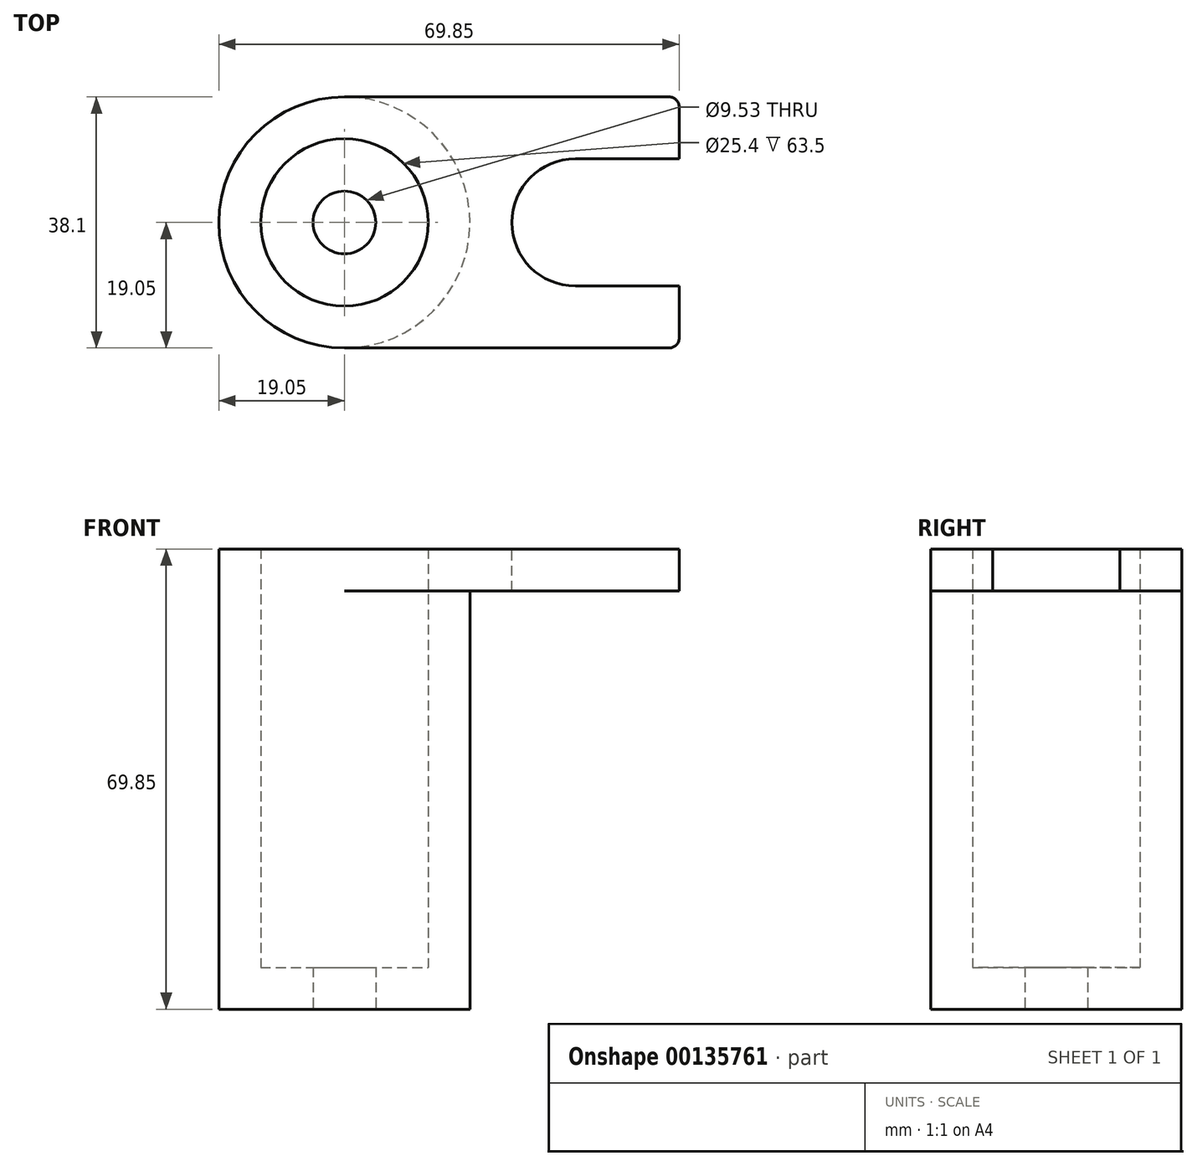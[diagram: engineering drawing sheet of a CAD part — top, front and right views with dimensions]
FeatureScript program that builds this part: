
annotation { "Feature Type Name" : "Feature", "Feature Type Description" : "" }
export const myFeature = defineFeature(function(context is Context, id is Id, definition is map)
    precondition{}
    {
        {
            var Q0;
            Q0=qCreatedBy(makeId("Front.planeOp"),FACE);
            var sketch = newSketch(context, id + "F0", { "sketchPlane" : qUnion([Q0])});
            skLineSegment(sketch, "E0", {"start": v(0, 0) * mm, "end": v(4.76, 0) * mm, "construction": true});
            skLineSegment(sketch, "E1", {"start": v(4.76, 0) * mm, "end": v(19.05, 0) * mm});
            skLineSegment(sketch, "E2", {"start": v(19.05, 0) * mm, "end": v(19.05, 69.85) * mm});
            skLineSegment(sketch, "E3", {"start": v(19.05, 69.85) * mm, "end": v(12.7, 69.85) * mm});
            skLineSegment(sketch, "E4", {"start": v(12.7, 69.85) * mm, "end": v(12.7, 6.35) * mm});
            skLineSegment(sketch, "E5", {"start": v(12.7, 6.35) * mm, "end": v(4.76, 6.35) * mm});
            skLineSegment(sketch, "E6", {"start": v(4.76, 6.35) * mm, "end": v(4.76, 0) * mm});
            skLineSegment(sketch, "E7", {"start": v(0, 0) * mm, "end": v(0, 69.85) * mm, "construction": true});
            skSolve(sketch);
        }
        {
            var Q0;
            Q0=makeQuery(id+"F0.imprint","IMPRINT",FACE,{"disambiguationData":[TD([[makeQuery(id+"F0.imprint","IMPRINT",EDGE,{"derivedFrom":sQuery(id+"F0.wireOp",EDGE,"E1")}),1.0]])]});
            var Q1;
            Q1=sQuery(id+"F0.wireOp",EDGE,"E7");
            revolve(context, id + "F1", {"entities" : qUnion([Q0]), "axis" : qUnion([Q1]), "revolveType" : RevolveType.FULL});
        }
        {
            var Q0;
            Q0=makeQuery(id+"F1.opRevolve","SWEPT_FACE",FACE,{"disambiguationData":[OSD([sQuery(id+"F0.wireOp",EDGE,"E3")])]});
            var sketch = newSketch(context, id + "F2", { "sketchPlane" : qUnion([Q0])});
            skCircle(sketch, "E8", {"center": v(0, 0) * mm, "radius": 12.7 * mm});
            skLineSegment(sketch, "E9", {"start": v(0, -19.05) * mm, "end": v(50.8, -19.05) * mm});
            skLineSegment(sketch, "E10", {"start": v(50.8, -19.05) * mm, "end": v(50.8, -9.65) * mm});
            skLineSegment(sketch, "E11", {"start": v(0, 19.05) * mm, "end": v(50.8, 19.05) * mm});
            skLineSegment(sketch, "E12", {"start": v(50.8, 19.05) * mm, "end": v(50.8, 9.65) * mm});
            skLineSegment(sketch, "E13", {"start": v(50.8, 9.65) * mm, "end": v(35.05, 9.65) * mm});
            skLineSegment(sketch, "E14", {"start": v(50.8, -9.65) * mm, "end": v(35.05, -9.65) * mm});
            skArc(sketch, "E15", {"start": v(35.05, -9.65) * mm, "mid": v(25.4, 0) * mm, "end": v(35.05, 9.65) * mm});
            skSolve(sketch);
        }
        {
            var Q0;
            {var subQ1=sQuery(id+"F2.wireOp",EDGE,"E9");Q0=makeQuery(id+"F2.imprint","IMPRINT",FACE,{"disambiguationData":[TD([[makeQuery(id+"F2.imprint","IMPRINT",EDGE,{"derivedFrom":subQ1}),1.0]])]});}
            extrude(context, id + "F3", {"entities" : qUnion([Q0]), "operationType" : NewBodyOperationType.ADD, "oppositeDirection" : true, "depth" : 6.35 * mm});
        }
        {
            var Q0;
            Q0=makeQuery(id+"FrmnFLm9WLYSRpA_1.1.F3.opExtrude","SWEPT_EDGE",EDGE,{"disambiguationData":[OSD([sQuery(id+"F2.wireOp",EDGE,"E9"),sQuery(id+"F2.wireOp",EDGE,"E10")])]});
            var Q1;
            Q1=makeQuery(id+"F3.opExtrude","SWEPT_EDGE",EDGE,{"disambiguationData":[OSD([sQuery(id+"F2.wireOp",EDGE,"E9"),sQuery(id+"F2.wireOp",EDGE,"E10")])]});
            var Q2;
            Q2=makeQuery(id+"F3.opExtrude","SWEPT_EDGE",EDGE,{"disambiguationData":[OSD([sQuery(id+"F2.wireOp",EDGE,"E11"),sQuery(id+"F2.wireOp",EDGE,"E12")])]});
            var Q3;
            Q3=makeQuery(id+"FrmnFLm9WLYSRpA_1.1.F3.opExtrude","SWEPT_EDGE",EDGE,{"disambiguationData":[OSD([sQuery(id+"F2.wireOp",EDGE,"E11"),sQuery(id+"F2.wireOp",EDGE,"E12")])]});
            fillet(context, id + "F4", {"entities" : qUnion([Q0, Q1, Q2, Q3]), "radius" : 1.52 * mm, "tangentPropagation" : true, "allowEdgeOverflow" : false});
        }
    });
